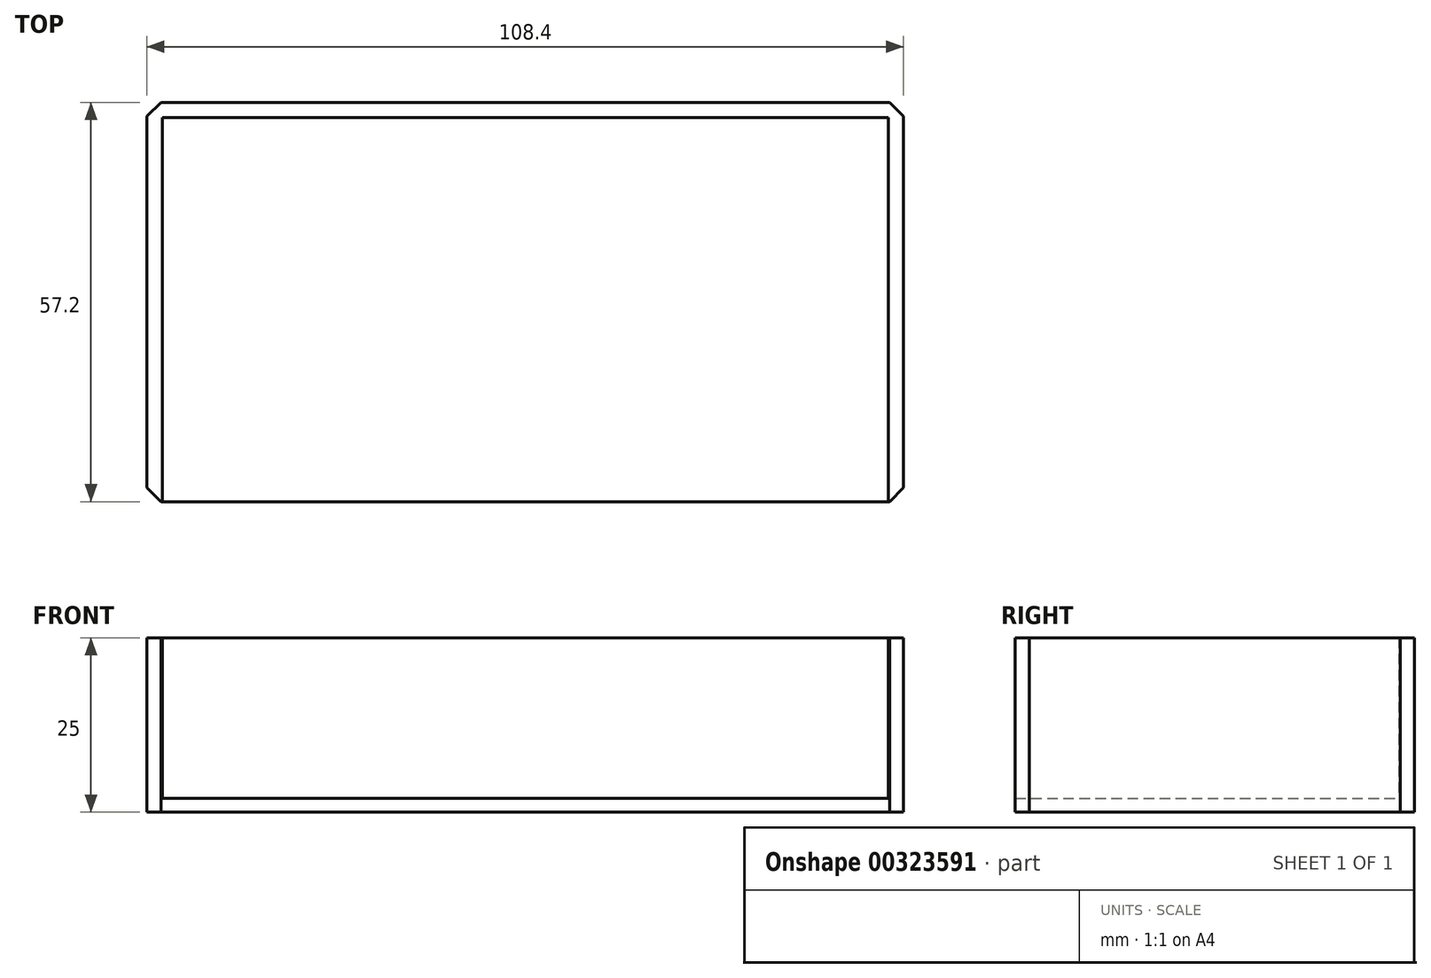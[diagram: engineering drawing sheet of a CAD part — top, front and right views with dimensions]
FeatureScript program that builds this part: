
annotation { "Feature Type Name" : "Feature", "Feature Type Description" : "" }
export const myFeature = defineFeature(function(context is Context, id is Id, definition is map)
    precondition{}
    {
        {
            var Q0;
            Q0=qCreatedBy(makeId("Top.planeOp"),FACE);
            var sketch = newSketch(context, id + "F0", { "sketchPlane" : qUnion([Q0])});
            skLineSegment(sketch, "E0.bottom", {"start": v(52, -27.5) * mm, "end": v(-52, -27.5) * mm});
            skLineSegment(sketch, "E0.top", {"start": v(52, 27.5) * mm, "end": v(-52, 27.5) * mm});
            skLineSegment(sketch, "E0.left", {"start": v(52, -27.5) * mm, "end": v(52, 27.5) * mm});
            skLineSegment(sketch, "E0.right", {"start": v(-52, -27.5) * mm, "end": v(-52, 27.5) * mm});
            skPoint(sketch, "E0.middle", {"position": v(0, 0) * mm});
            skLineSegment(sketch, "E1.0", {"start": v(-54.2, -27.5) * mm, "end": v(-54.2, 29.7) * mm});
            skLineSegment(sketch, "E1.1", {"start": v(54.2, 29.7) * mm, "end": v(-54.2, 29.7) * mm});
            skLineSegment(sketch, "E1.2", {"start": v(54.2, -27.5) * mm, "end": v(54.2, 29.7) * mm});
            skLineSegment(sketch, "E2", {"start": v(-54.2, -27.5) * mm, "end": v(-52, -27.5) * mm});
            skLineSegment(sketch, "E3", {"start": v(52, -27.5) * mm, "end": v(54.2, -27.5) * mm});
            skSolve(sketch);
        }
        {
            var Q0;
            Q0=makeQuery(id+"F0.imprint","IMPRINT",FACE,{"disambiguationData":[TD([[makeQuery(id+"F0.imprint","IMPRINT",EDGE,{"derivedFrom":sQuery(id+"F0.wireOp",EDGE,"E0.bottom")}),-1.0]])]});
            extrude(context, id + "F1", {"entities" : qUnion([Q0]), "depth" : 2 * mm});
        }
        {
            var Q0;
            Q0=makeQuery(id+"F0.imprint","IMPRINT",FACE,{"disambiguationData":[TD([[makeQuery(id+"F0.imprint","IMPRINT",EDGE,{"derivedFrom":sQuery(id+"F0.wireOp",EDGE,"E0.top")}),-1.0]])]});
            extrude(context, id + "F2", {"entities" : qUnion([Q0]), "operationType" : NewBodyOperationType.ADD, "depth" : 25 * mm});
        }
        {
            var Q0;
            Q0=makeQuery(id+"F2.opExtrude","SWEPT_EDGE",EDGE,{"disambiguationData":[OSD([sQuery(id+"F0.wireOp",EDGE,"E1.1"),sQuery(id+"F0.wireOp",EDGE,"E1.2")])]});
            var Q1;
            Q1=makeQuery(id+"F2.opExtrude","SWEPT_EDGE",EDGE,{"disambiguationData":[OSD([sQuery(id+"F0.wireOp",EDGE,"E1.0"),sQuery(id+"F0.wireOp",EDGE,"E1.1")])]});
            var Q2;
            Q2=makeQuery(id+"F2.opExtrude","SWEPT_EDGE",EDGE,{"disambiguationData":[OSD([sQuery(id+"F0.wireOp",EDGE,"E1.0"),sQuery(id+"F0.wireOp",EDGE,"E2")])]});
            var Q3;
            Q3=makeQuery(id+"F2.opExtrude","SWEPT_EDGE",EDGE,{"disambiguationData":[OSD([sQuery(id+"F0.wireOp",EDGE,"E1.2"),sQuery(id+"F0.wireOp",EDGE,"E3")])]});
            chamfer(context, id + "F3", {"entities" : qUnion([Q0, Q1, Q2, Q3]), "width" : 2 * mm, "tangentPropagation" : true});
        }
    });
